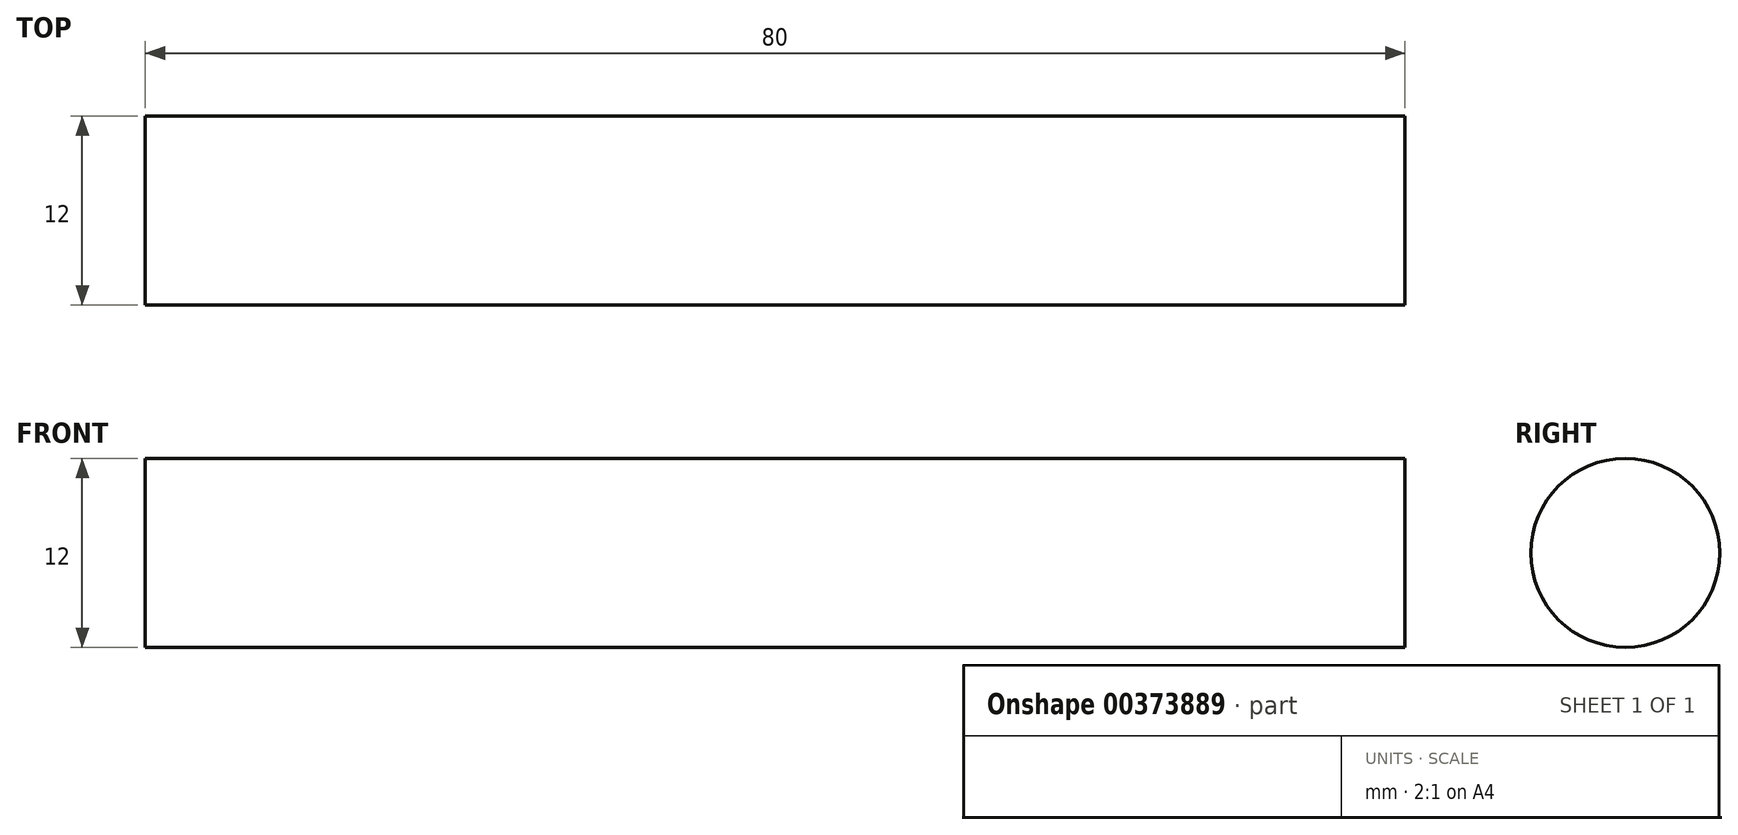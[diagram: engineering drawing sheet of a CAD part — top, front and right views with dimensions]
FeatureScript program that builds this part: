
annotation { "Feature Type Name" : "Feature", "Feature Type Description" : "" }
export const myFeature = defineFeature(function(context is Context, id is Id, definition is map)
    precondition{}
    {
        {
            var Q0;
            Q0=qCreatedBy(makeId("Right.planeOp"),FACE);
            var sketch = newSketch(context, id + "F0", { "sketchPlane" : qUnion([Q0])});
            skCircle(sketch, "E0", {"center": v(25.13, 13.04) * mm, "radius": 6 * mm});
            skSolve(sketch);
        }
        {
            var Q0;
            Q0 = qSketchRegion(id + "F0", true);
            extrude(context, id + "F1", {"entities" : qUnion([Q0]), "depth" : 80 * mm, "offsetDistance" : 25 * mm});
        }
    });
